# Revit family: Kabelrinne_rksm_A2_610_615_620_630_640_650_660
name_source: partatom
category: Generic Models
revit_build: Autodesk Revit 2017 (Build: 20160225_1515(x64)
units: mm (PartAtom-declared; Revit-internal decimal feet)

## family parameters
Always vertical = Yes
Can host rebar = No
Cut with Voids When Loaded = No
Part Type = Normal
Room Calculation Point = No
Round Connector Dimension = Use Diameter
Shared = No
Work Plane-Based = No

## types (7) — shared parameters
Cut's number = 29
Cut's number 2 = 2
Cut's number 3 = 58
Cut's space = 102 mm
Cut's space 2 = 51 mm
Length = 3000 mm  [stored 9.84252 ft]
Manufacturer = OBO BETTERMANN
Material = Stainless steel, A2
URL = http://www.obo-bettermann.com

## per-type parameters (varying)
| type | GTIN | Manufacturer Art.No. | Width | Width 1 |
| RKSM 610 A2 | 4012195706083 | 6047613 | 100 mm  [stored 0.328084 ft] | 50 mm  [stored 0.164042 ft] |
| RKSM 615 A2 | 4012195706120 | 6047632 | 150 mm | 75 mm |
| RKSM 620 A2 | 4012195706144 | 6047640 | 200 mm  [stored 0.656168 ft] | 100 mm  [stored 0.328084 ft] |
| RKSM 630 A2 | 4012195706182 | 6047656 | 300 mm | 150 mm |
| RKSM 640 A2 | 4012195706205 | 6047691 | 400 mm  [stored 1.31234 ft] | 200 mm  [stored 0.656168 ft] |
| RKSM 650 A2 | 4012195706243 | 6047721 | 500 mm  [stored 1.64042 ft] | 250 mm  [stored 0.82021 ft] |
| RKSM 660 A2 | 4012195706267 | 6047737 | 600 mm | 300 mm |

note: column(s) folded — value = type name in every type: Article Type

note: [stored X ft] marks values corroborated as IEEE doubles in the binary element streams (Revit-internal decimal feet)

## geometry (parser evidence)
native form markers: Sweep x1
no freeform markers — native parametric forms only
